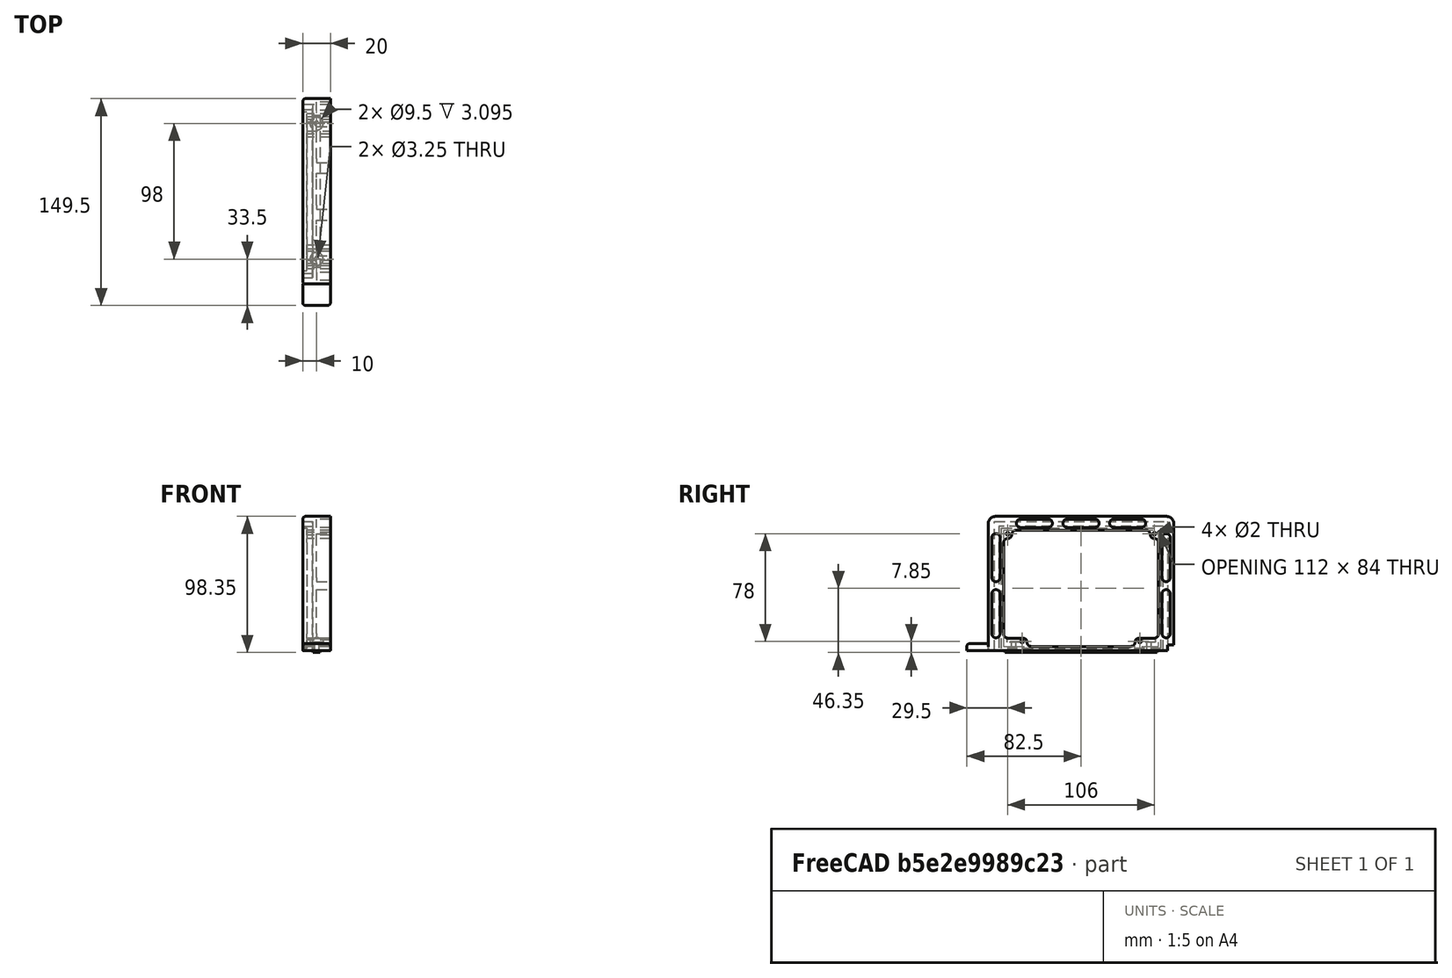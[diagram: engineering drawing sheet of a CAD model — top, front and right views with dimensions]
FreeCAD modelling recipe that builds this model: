
FCSTD DOCUMENT  (FreeCAD 0.18R)
Label: K-MINI-Enclosure-TopHandleV2
License: CreativeCommons Attribution
LicenseURL: http://creativecommons.org/licenses/by/4.0/
objects: Sketcher::SketchObject×8, PartDesign::Pocket×4, PartDesign::Pad×3, PartDesign::Fillet×2, PartDesign::Body×2, Mesh::Feature×2, PartDesign::Hole×1, Part::Mirroring×1, Part::MultiFuse×1, App::Part×1
note: 30 computed .brp shape members not serialized (recipe doc carries the construction recipe); baked Part::Feature solids carry a one-line shape summary decoded from their .brp

FEATURE [Sketcher::SketchObject] Sketch  label="BaseProfile"
  MapMode = 5
  Placement = pos=(0,0,0) rot=(0.57735,0.57735,0.57735;2.0944rad)
  Support = -> [YZ_Plane]
  sketch-geometry (27):
    g0: LineSegment StartX=-7 StartY=0 StartZ=0 EndX=-7 EndY=92 EndZ=0
    g1: ArcOfCircle CenterX=-2 CenterY=92 CenterZ=0 NormalX=0 NormalY=0 NormalZ=1 AngleXU=0 Radius=5 StartAngle=1.5708 EndAngle=3.14159
    g2: LineSegment StartX=-2 StartY=97 StartZ=0 EndX=122 EndY=97 EndZ=0
    g3: ArcOfCircle CenterX=122 CenterY=92 CenterZ=0 NormalX=0 NormalY=0 NormalZ=1 AngleXU=0 Radius=5 StartAngle=2e-16 EndAngle=1.5708
    g4: LineSegment StartX=127 StartY=92 StartZ=0 EndX=127 EndY=4.1 EndZ=0
    g5: LineSegment StartX=122.5 StartY=0 StartZ=0 EndX=-7 EndY=0 EndZ=0
    g6: LineSegment StartX=4 StartY=12 StartZ=0 EndX=4 EndY=78 EndZ=0
    g7: LineSegment StartX=13 StartY=87 StartZ=0 EndX=107 EndY=87 EndZ=0
    g8: LineSegment StartX=116 StartY=78 StartZ=0 EndX=116 EndY=12 EndZ=0
    g9: ArcOfCircle CenterX=107 CenterY=84 CenterZ=0 NormalX=0 NormalY=0 NormalZ=1 AngleXU=0 Radius=3 StartAngle=0 EndAngle=1.5708
    g10: LineSegment [constr] StartX=60 StartY=116.041 StartZ=0 EndX=60 EndY=-23.3593 EndZ=0
    g11: LineSegment StartX=122.5 StartY=0 StartZ=0 EndX=122.5 EndY=4.1 EndZ=0
    g12: LineSegment StartX=122.5 StartY=4.1 StartZ=0 EndX=127 EndY=4.1 EndZ=0
    g13: ArcOfCircle CenterX=24 CenterY=6 CenterZ=0 NormalX=0 NormalY=0 NormalZ=1 AngleXU=0 Radius=3 StartAngle=3.14159 EndAngle=4.71239
    g14: ArcOfCircle CenterX=96 CenterY=6 CenterZ=0 NormalX=0 NormalY=0 NormalZ=1 AngleXU=0 Radius=3 StartAngle=4.71239 EndAngle=6.28319
    g15: ArcOfCircle CenterX=102 CenterY=6 CenterZ=0 NormalX=0 NormalY=0 NormalZ=1 AngleXU=0 Radius=3 StartAngle=1.5708 EndAngle=3.14159
    g16: LineSegment StartX=24 StartY=3 StartZ=0 EndX=96 EndY=3 EndZ=0
    g17: ArcOfCircle CenterX=18 CenterY=6 CenterZ=0 NormalX=0 NormalY=0 NormalZ=1 AngleXU=0 Radius=3 StartAngle=0 EndAngle=1.5708
    g18: ArcOfCircle CenterX=7 CenterY=84 CenterZ=0 NormalX=0 NormalY=0 NormalZ=1 AngleXU=0 Radius=3 StartAngle=4.71239 EndAngle=6.28319
    g19: ArcOfCircle CenterX=7 CenterY=78 CenterZ=0 NormalX=0 NormalY=0 NormalZ=1 AngleXU=0 Radius=3 StartAngle=1.5708 EndAngle=3.14159
    g20: ArcOfCircle CenterX=13 CenterY=84 CenterZ=0 NormalX=0 NormalY=0 NormalZ=1 AngleXU=0 Radius=3 StartAngle=1.5708 EndAngle=3.14159
    g21: ArcOfCircle CenterX=113 CenterY=84 CenterZ=0 NormalX=0 NormalY=0 NormalZ=1 AngleXU=0 Radius=3 StartAngle=3.14159 EndAngle=4.71239
    g22: ArcOfCircle CenterX=113 CenterY=78 CenterZ=0 NormalX=0 NormalY=0 NormalZ=1 AngleXU=0 Radius=3 StartAngle=-1.8e-15 EndAngle=1.5708
    g23: LineSegment StartX=102 StartY=9 StartZ=0 EndX=113 EndY=9 EndZ=0
    g24: ArcOfCircle CenterX=113 CenterY=12 CenterZ=0 NormalX=0 NormalY=0 NormalZ=1 AngleXU=0 Radius=3 StartAngle=4.71239 EndAngle=6.28319
    g25: LineSegment StartX=7 StartY=9 StartZ=0 EndX=18 EndY=9 EndZ=0
    g26: ArcOfCircle CenterX=7 CenterY=12 CenterZ=0 NormalX=0 NormalY=0 NormalZ=1 AngleXU=0 Radius=3 StartAngle=3.14159 EndAngle=4.71239
  constraints (70):
    c: Tangent(g0,g1) = 1.5708
    c: Tangent(g1,g2) = 1.5708
    c: Tangent(g2,g3) = 1.5708
    c: Tangent(g3,g4) = 1.5708
    c: Coincident(g5,g0)
    c: Horizontal(g2)
    c: Vertical(g0)
    c: Vertical(g4)
    c: Radius(g1) = 5
    c: Equal(g1,g3)
    c: Tangent(g7,g9) = 1.5708
    c: Vertical(g6)
    c: Vertical(g8)
    c: Horizontal(g7)
    c: DistanceX(g0,g-1) = 7
    c: Horizontal(g5)
    c: DistanceY(g-1,g1) = 97
    c: Radius(g9) = 3
    c: PointOnObject(g0,g-1)
    c: DistanceX(g-1,g10) = 60
    c: Symmetric(g6,g8,g10)
    c: Coincident(g11,g12)
    c: Coincident(g4,g12)
    c: Coincident(g5,g11)
    c: Vertical(g11)
    c: Horizontal(g12)
    c: DistanceY(g5,g11) = 4.1
    c: DistanceX(g0,g4) = 134
    c: Tangent(g15,g14) = 1.5708
    c: Tangent(g14,g16) = -1.5708
    c: Tangent(g16,g13) = -1.5708
    c: Horizontal(g16)
    c: DistanceX(g12,g12) = 4.5
    c: Horizontal(g17,g17)
    c: Vertical(g17,g17)
    c: Tangent(g17,g13) = 1.5708
    c: Equal(g13,g17)
    c: Horizontal(g14,g15)
    c: Equal(g15,g14)
    c: Horizontal(g18,g18)
    c: Vertical(g18,g18)
    c: Tangent(g19,g6) = 1.5708
    c: Tangent(g19,g18) = 1.5708
    c: Equal(g19,g18)
    c: Tangent(g7,g20) = 1.5708
    c: Tangent(g18,g20) = 1.5708
    c: Equal(g18,g20)
    c: Equal(g13,g14)
    c: Tangent(g22,g8) = 1.5708
    c: Vertical(g21,g21)
    c: Horizontal(g21,g21)
    c: Tangent(g21,g22) = 1.5708
    c: Tangent(g9,g21) = 1.5708
    c: Equal(g9,g21)
    c: Equal(g21,g22)
    c: Tangent(g15,g23) = 1.5708
    c: Horizontal(g23)
    c: Tangent(g23,g24) = -1.5708
    c: Tangent(g8,g24) = 1.5708
    c: Equal(g15,g24)
    c: Tangent(g25,g17) = 1.5708
    c: Tangent(g6,g26) = 1.5708
    c: Tangent(g25,g26) = -1.5708
    c: Symmetric(g13,g14,g10)
    c: DistanceY(g0,g7) = 87
    c: DistanceX(g6,g8) = 112
    c: Equal(g20,g9)
    c: DistanceY(g-1,g13) = 3
    c: DistanceX(g25,g25) = 11
    c: Radius(g24) = 3
FEATURE [PartDesign::Pad] Pad  label="RawHandle"
  Length = 20
  Length2 = 100
  Placement = pos=(0,0,0) rot=(0.57735,0.57735,0.57735;2.0944rad)
  Profile = -> Sketch
  Type = 0
FEATURE [Sketcher::SketchObject] Sketch001  label="TopFRCutoutProfile"
  MapMode = 5
  Placement = pos=(20,-1.8e-14,1.1e-14) rot=(0.57735,0.57735,0.57735;2.0944rad)
  sketch-geometry (9):
    g0: LineSegment StartX=-2.5 StartY=0 StartZ=0 EndX=-2.5 EndY=93.2 EndZ=0
    g1: LineSegment StartX=-2.5 StartY=93.2 StartZ=0 EndX=122.5 EndY=93.2 EndZ=0
    g2: LineSegment StartX=122.5 StartY=93.2 StartZ=0 EndX=122.5 EndY=0 EndZ=0
    g3: LineSegment StartX=122.5 StartY=0 StartZ=0 EndX=119.3 EndY=0 EndZ=0
    g4: LineSegment StartX=119.3 StartY=0 StartZ=0 EndX=119.3 EndY=90 EndZ=0
    g5: LineSegment StartX=119.3 StartY=90 StartZ=0 EndX=0.7 EndY=90 EndZ=0
    g6: LineSegment StartX=0.7 StartY=90 StartZ=0 EndX=0.7 EndY=0 EndZ=0
    g7: LineSegment StartX=0.7 StartY=0 StartZ=0 EndX=-2.5 EndY=0 EndZ=0
    g8: LineSegment [constr] StartX=60 StartY=110 StartZ=0 EndX=60 EndY=0 EndZ=0
  constraints (26):
    c: Coincident(g0,g1)
    c: Coincident(g1,g2)
    c: Coincident(g2,g3)
    c: Coincident(g3,g4)
    c: Coincident(g4,g5)
    c: Coincident(g5,g6)
    c: Coincident(g6,g7)
    c: Horizontal(g7)
    c: Horizontal(g3)
    c: Horizontal(g1)
    c: Horizontal(g5)
    c: Vertical(g0)
    c: Vertical(g6)
    c: Vertical(g4)
    c: Vertical(g2)
    c: DistanceY(g4,g1) = 3.2
    c: DistanceX(g3,g3) = 3.2
    c: DistanceY(g6,g5) = 90
    c: DistanceX(g0,g2) = 125  'coverwidth'
    c: DistanceX(g-1,g8) = 60
    c: Coincident(g0,g7)
    c: PointOnObject(g6,g-1)
    c: Symmetric(g6,g3,g8)
    c: Symmetric(g0,g2,g8)
    c: PointOnObject(g8,g-1)
    c: DistanceY(g8,g8) = 110
FEATURE [PartDesign::Pocket] Pocket  label="TopFRPanelMount"
  BaseFeature = -> Pad
  Length = 7
  Length2 = 100
  Placement = pos=(0,0,0) rot=(0.57735,0.57735,0.57735;2.0944rad)
  Profile = -> Sketch001
  Type = 0
FEATURE [Sketcher::SketchObject] Sketch002  label="SlotProfile"
  Placement = pos=(0,0,-1.04e-13) rot=(0.707107,0.707107,0;3.14159rad)
  sketch-geometry (4):
    g0: LineSegment StartX=5 StartY=12.5 StartZ=0 EndX=115 EndY=12.5 EndZ=0
    g1: LineSegment StartX=115 StartY=12.5 StartZ=0 EndX=115 EndY=7.5 EndZ=0
    g2: LineSegment StartX=115 StartY=7.5 StartZ=0 EndX=5 EndY=7.5 EndZ=0
    g3: LineSegment StartX=5 StartY=7.5 StartZ=0 EndX=5 EndY=12.5 EndZ=0
  constraints (12):
    c: Coincident(g0,g1)
    c: Coincident(g1,g2)
    c: Coincident(g2,g3)
    c: Coincident(g3,g0)
    c: Horizontal(g0)
    c: Horizontal(g2)
    c: Vertical(g1)
    c: Vertical(g3)
    c: DistanceX(g-1,g2) = 5
    c: DistanceX(g2,g2) = 110
    c: DistanceY(g3,g3) = 5
    c: DistanceY(g-1,g2) = 7.5
FEATURE [Sketcher::SketchObject] Sketch004  label="M2Screwpositions"
  MapMode = 5
  Placement = pos=(20,-2.7e-14,1.6e-14) rot=(0.57735,0.57735,0.57735;2.0944rad)
  sketch-geometry (5):
    g0: Circle CenterX=7 CenterY=84.5 CenterZ=0 NormalX=0 NormalY=0 NormalZ=1 AngleXU=0 Radius=1
    g1: Circle CenterX=113 CenterY=84.5 CenterZ=0 NormalX=0 NormalY=0 NormalZ=1 AngleXU=0 Radius=1
    g2: Circle CenterX=17.5 CenterY=6.5 CenterZ=0 NormalX=0 NormalY=0 NormalZ=1 AngleXU=0 Radius=1
    g3: Circle CenterX=102.5 CenterY=6.5 CenterZ=0 NormalX=0 NormalY=0 NormalZ=1 AngleXU=0 Radius=1
    g4: LineSegment [constr] StartX=60 StartY=121.121 StartZ=0 EndX=60 EndY=-12.2493 EndZ=0
  constraints (11):
    c: Radius(g0) = 1
    c: Equal(g0,g1)
    c: Equal(g0,g2)
    c: DistanceY(g-1,g2) = 6.5
    c: DistanceY(g2,g0) = 78
    c: Horizontal(g0,g1)
    c: DistanceX(g-1,g4) = 60
    c: Symmetric(g2,g3,g4)
    c: DistanceX(g0,g1) = 106
    c: DistanceX(g2,g3) = 85
    c: Symmetric(g1,g0,g4)
FEATURE [Sketcher::SketchObject] Sketch005  label="Ovals"
  MapMode = 5
  Placement = pos=(0,0,0) rot=(0.57735,0.57735,-0.57735;4.18879rad)
  Support = -> [Pocket]
  sketch-geometry (29):
    g0: ArcOfCircle CenterX=-1.5 CenterY=-12.2603 CenterZ=0 NormalX=0 NormalY=0 NormalZ=1 AngleXU=0 Radius=3 StartAngle=3e-16 EndAngle=3.14159
    g1: ArcOfCircle CenterX=-1.5 CenterY=-41.0407 CenterZ=0 NormalX=0 NormalY=0 NormalZ=1 AngleXU=0 Radius=3 StartAngle=3.14159 EndAngle=6.28319
    g2: LineSegment StartX=-4.5 StartY=-12.2603 StartZ=0 EndX=-4.5 EndY=-41.0407 EndZ=0
    g3: LineSegment StartX=1.5 StartY=-12.2603 StartZ=0 EndX=1.5 EndY=-41.0407 EndZ=0
    g4: ArcOfCircle CenterX=-1.5 CenterY=-52.7873 CenterZ=0 NormalX=0 NormalY=0 NormalZ=1 AngleXU=0 Radius=3 StartAngle=-9e-16 EndAngle=3.14159
    g5: ArcOfCircle CenterX=-1.5 CenterY=-81.5678 CenterZ=0 NormalX=0 NormalY=0 NormalZ=1 AngleXU=0 Radius=3 StartAngle=3.14159 EndAngle=6.28319
    g6: LineSegment StartX=-4.5 StartY=-52.7873 StartZ=0 EndX=-4.5 EndY=-81.5678 EndZ=0
    g7: LineSegment StartX=1.5 StartY=-52.7873 StartZ=0 EndX=1.5 EndY=-81.5678 EndZ=0
    g8: ArcOfCircle CenterX=16.2869 CenterY=-92 CenterZ=0 NormalX=0 NormalY=0 NormalZ=1 AngleXU=0 Radius=3 StartAngle=1.5708 EndAngle=4.71239
    g9: ArcOfCircle CenterX=36.2869 CenterY=-92 CenterZ=0 NormalX=0 NormalY=0 NormalZ=1 AngleXU=0 Radius=3 StartAngle=4.71239 EndAngle=7.85398
    g10: LineSegment StartX=16.2869 StartY=-95 StartZ=0 EndX=36.2869 EndY=-95 EndZ=0
    g11: LineSegment StartX=16.2869 StartY=-89 StartZ=0 EndX=36.2869 EndY=-89 EndZ=0
    g12: ArcOfCircle CenterX=50 CenterY=-92 CenterZ=0 NormalX=0 NormalY=0 NormalZ=1 AngleXU=0 Radius=3 StartAngle=1.5708 EndAngle=4.71239
    g13: ArcOfCircle CenterX=70 CenterY=-92 CenterZ=0 NormalX=0 NormalY=0 NormalZ=1 AngleXU=0 Radius=3 StartAngle=4.71239 EndAngle=7.85398
    g14: LineSegment StartX=50 StartY=-95 StartZ=0 EndX=70 EndY=-95 EndZ=0
    g15: LineSegment StartX=50 StartY=-89 StartZ=0 EndX=70 EndY=-89 EndZ=0
    g16: ArcOfCircle CenterX=83.7131 CenterY=-92 CenterZ=0 NormalX=0 NormalY=0 NormalZ=1 AngleXU=0 Radius=3 StartAngle=1.5708 EndAngle=4.71239
    g17: ArcOfCircle CenterX=103.713 CenterY=-92 CenterZ=0 NormalX=0 NormalY=0 NormalZ=1 AngleXU=0 Radius=3 StartAngle=4.71239 EndAngle=7.85398
    g18: LineSegment StartX=83.7131 StartY=-95 StartZ=0 EndX=103.713 EndY=-95 EndZ=0
    g19: LineSegment StartX=83.7131 StartY=-89 StartZ=0 EndX=103.713 EndY=-89 EndZ=0
    g20: ArcOfCircle CenterX=121.5 CenterY=-81.5678 CenterZ=0 NormalX=0 NormalY=0 NormalZ=1 AngleXU=0 Radius=3 StartAngle=3.14159 EndAngle=6.28319
    g21: ArcOfCircle CenterX=121.5 CenterY=-52.7873 CenterZ=0 NormalX=0 NormalY=0 NormalZ=1 AngleXU=0 Radius=3 StartAngle=2e-16 EndAngle=3.14159
    g22: LineSegment StartX=124.5 StartY=-81.5678 StartZ=0 EndX=124.5 EndY=-52.7873 EndZ=0
    g23: LineSegment StartX=118.5 StartY=-81.5678 StartZ=0 EndX=118.5 EndY=-52.7873 EndZ=0
    g24: ArcOfCircle CenterX=121.5 CenterY=-41.0407 CenterZ=0 NormalX=0 NormalY=0 NormalZ=1 AngleXU=0 Radius=3 StartAngle=3.14159 EndAngle=6.28319
    g25: ArcOfCircle CenterX=121.5 CenterY=-12.2603 CenterZ=0 NormalX=0 NormalY=0 NormalZ=1 AngleXU=0 Radius=3 StartAngle=0 EndAngle=3.14159
    g26: LineSegment StartX=124.5 StartY=-41.0407 StartZ=0 EndX=124.5 EndY=-12.2603 EndZ=0
    g27: LineSegment StartX=118.5 StartY=-41.0407 StartZ=0 EndX=118.5 EndY=-12.2603 EndZ=0
    g28: LineSegment [constr] StartX=60 StartY=32.8445 StartZ=0 EndX=60 EndY=-124.528 EndZ=0
  constraints (65):
    c: Tangent(g0,g3) = 1.5708
    c: Tangent(g0,g2) = -1.5708
    c: Tangent(g2,g1) = -1.5708
    c: Tangent(g3,g1) = 1.5708
    c: Vertical(g2)
    c: Equal(g0,g1)
    c: Tangent(g4,g7) = 1.5708
    c: Tangent(g4,g6) = -1.5708
    c: Tangent(g6,g5) = -1.5708
    c: Tangent(g7,g5) = 1.5708
    c: Vertical(g6)
    c: Equal(g4,g5)
    c: Tangent(g8,g11) = 1.5708
    c: Tangent(g8,g10) = -1.5708
    c: Tangent(g10,g9) = -1.5708
    c: Tangent(g11,g9) = 1.5708
    c: Horizontal(g10)
    c: Equal(g8,g9)
    c: Tangent(g12,g15) = 1.5708
    c: Tangent(g12,g14) = -1.5708
    c: Tangent(g14,g13) = -1.5708
    c: Tangent(g15,g13) = 1.5708
    c: Horizontal(g14)
    c: Equal(g12,g13)
    c: Tangent(g16,g19) = 1.5708
    c: Tangent(g16,g18) = -1.5708
    c: Tangent(g18,g17) = -1.5708
    c: Tangent(g19,g17) = 1.5708
    c: Horizontal(g18)
    c: Equal(g16,g17)
    c: Tangent(g20,g23) = 1.5708
    c: Tangent(g20,g22) = -1.5708
    c: Tangent(g22,g21) = -1.5708
    c: Tangent(g23,g21) = 1.5708
    c: Vertical(g22)
    c: Equal(g20,g21)
    c: Tangent(g24,g27) = 1.5708
    c: Tangent(g24,g26) = -1.5708
    c: Tangent(g26,g25) = -1.5708
    c: Tangent(g27,g25) = 1.5708
    c: Vertical(g26)
    c: Equal(g24,g25)
    c: Horizontal(g8,g12)
    c: Vertical(g0,g4)
    c: Vertical(g25,g21)
    c: Equal(g3,g7)
    c: Equal(g7,g27)
    c: Equal(g27,g23)
    c: Radius(g5) = 3
    c: Equal(g5,g1)
    c: Equal(g5,g24)
    c: Equal(g5,g20)
    c: Horizontal(g5,g20)
    c: DistanceX(g-1,g28) = 60
    c: Symmetric(g0,g25,g28)
    c: Symmetric(g13,g12,g28)
    c: Symmetric(g9,g16,g28)
    c: Equal(g10,g18)
    c: Equal(g18,g14)
    c: Radius(g9) = 3
    c: Equal(g9,g13)
    c: Equal(g9,g17)
    c: DistanceY(g8,g-1) = 92
    c: DistanceX(g0,g25) = 123
    c: DistanceX(g12,g13) = 20
FEATURE [PartDesign::Pocket] Pocket003  label="DesignElements"
  BaseFeature = -> Pocket
  Length = 10
  Length2 = 100
  Placement = pos=(0,0,0) rot=(0.57735,0.57735,0.57735;2.0944rad)
  Profile = -> Sketch005
  Type = 0
FEATURE [PartDesign::Pad] Pad001  label="SlotRail"
  BaseFeature = -> Pocket003
  Length = 1.35
  Length2 = 100
  Placement = pos=(0,0,0) rot=(0.57735,0.57735,0.57735;2.0944rad)
  Profile = -> Sketch002
  Type = 0
FEATURE [PartDesign::Pocket] Pocket004  label="M2Holes"
  BaseFeature = -> Pad001
  Length = 20
  Length2 = 100
  Placement = pos=(0,0,0) rot=(0.57735,0.57735,0.57735;2.0944rad)
  Profile = -> Sketch004
  Type = 0
FEATURE [Sketcher::SketchObject] Sketch003  label="SideCoverArea"
  MapMode = 5
  Placement = pos=(20,-4.4e-15,4.4e-15) rot=(0.57735,0.57735,0.57735;2.0944rad)
  Support = -> [Pocket004]
  sketch-geometry (5):
    g0: LineSegment StartX=2.5 StartY=88.5 StartZ=0 EndX=117.5 EndY=88.5 EndZ=0
    g1: LineSegment StartX=117.5 StartY=88.5 StartZ=0 EndX=117.5 EndY=1.5 EndZ=0
    g2: LineSegment StartX=117.5 StartY=1.5 StartZ=0 EndX=2.5 EndY=1.5 EndZ=0
    g3: LineSegment StartX=2.5 StartY=1.5 StartZ=0 EndX=2.5 EndY=88.5 EndZ=0
    g4: LineSegment [constr] StartX=60 StartY=123.567 StartZ=0 EndX=60 EndY=-13.9522 EndZ=0
  constraints (13):
    c: Coincident(g0,g1)
    c: Coincident(g1,g2)
    c: Coincident(g2,g3)
    c: Coincident(g3,g0)
    c: Horizontal(g0)
    c: Horizontal(g2)
    c: Vertical(g1)
    c: Vertical(g3)
    c: DistanceX(g2,g2) = 115
    c: DistanceY(g-1,g2) = 1.5
    c: DistanceY(g3,g3) = 87
    c: DistanceX(g-1,g4) = 60
    c: Symmetric(g0,g0,g4)
FEATURE [PartDesign::Pocket] Pocket005  label="SideCoverCutout"
  BaseFeature = -> Pocket004
  Length = 3
  Length2 = 100
  Placement = pos=(0,0,0) rot=(0.57735,0.57735,0.57735;2.0944rad)
  Profile = -> Sketch003
  Type = 0
FEATURE [Sketcher::SketchObject] Sketch006  label="ExtrusionScrewPos"
  Placement = pos=(0,3e-15,10) rot=(0,0,-1;1.5708rad)
  Support = -> [Pocket004]
  sketch-geometry (3):
    g0: LineSegment [constr] StartX=-60 StartY=94.2757 StartZ=0 EndX=-60 EndY=-53.0118 EndZ=0
    g1: Circle CenterX=-109 CenterY=10 CenterZ=0 NormalX=0 NormalY=0 NormalZ=1 AngleXU=0 Radius=1.75
    g2: Circle CenterX=-11 CenterY=10 CenterZ=0 NormalX=0 NormalY=0 NormalZ=1 AngleXU=0 Radius=1.75
  constraints (7):
    c: Vertical(g0)
    c: Radius(g1) = 1.75
    c: Equal(g1,g2)
    c: Symmetric(g1,g2,g0)
    c: DistanceY(g-1,g1) = 10
    c: DistanceX(g1,g2) = 98
    c: DistanceX(g0,g-1) = 60
FEATURE [PartDesign::Hole] Hole
  BaseFeature = -> Pocket005
  Depth = 25
  DepthType = 0
  Diameter = 3.25
  DrillPoint = 1
  DrillPointAngle = 118
  HoleCutCountersinkAngle = 90
  HoleCutDepth = 4
  HoleCutDiameter = 9.5
  HoleCutType = 1
  ModelActualThread = false
  Placement = pos=(0,0,0) rot=(0.57735,0.57735,0.57735;2.0944rad)
  Profile = -> Sketch006
  Tapered = false
  TaperedAngle = 90
  ThreadAngle = 0
  ThreadClass = 0
  ThreadCutOffInner = 0
  ThreadCutOffOuter = 0
  ThreadDirection = 0
  ThreadFit = 0
  ThreadPitch = 0
  ThreadSize = 0
  ThreadType = 0
  Threaded = false
FEATURE [Sketcher::SketchObject] Sketch007
  MapMode = 5
  Placement = pos=(0,0,0) rot=(0.57735,0.57735,0.57735;2.0944rad)
  Support = -> [YZ_Plane002]
  sketch-geometry (5):
    g0: LineSegment StartX=-7 StartY=0 StartZ=0 EndX=-22.5 EndY=0 EndZ=0
    g1: LineSegment StartX=-22.5 StartY=0 StartZ=0 EndX=-22.5 EndY=3 EndZ=0
    g2: ArcOfCircle CenterX=-20.5 CenterY=3 CenterZ=0 NormalX=0 NormalY=0 NormalZ=1 AngleXU=0 Radius=2 StartAngle=1.5708 EndAngle=3.14159
    g3: LineSegment StartX=-20.5 StartY=5 StartZ=0 EndX=-7 EndY=5 EndZ=0
    g4: LineSegment StartX=-7 StartY=5 StartZ=0 EndX=-7 EndY=0 EndZ=0
  constraints (14):
    c: Coincident(g0,g1)
    c: Tangent(g1,g2) = 1.5708
    c: Tangent(g2,g3) = 1.5708
    c: Coincident(g3,g4)
    c: Coincident(g4,g0)
    c: Vertical(g4)
    c: Horizontal(g3)
    c: Vertical(g1)
    c: Horizontal(g0)
    c: PointOnObject(g0,g-1)
    c: DistanceX(g0,g-1) = 7
    c: DistanceY(g-1,g3) = 5
    c: DistanceX(g0,g-1) = 22.5
    c: Radius(g2) = 2
FEATURE [PartDesign::Pad] Pad002
  Length = 20
  Length2 = 100
  Placement = pos=(0,0,0) rot=(0.57735,0.57735,0.57735;2.0944rad)
  Profile = -> Sketch007
  Type = 0
FEATURE [PartDesign::Fillet] Fillet
  Base = -> Pad002 [Edge7,Edge12]
  BaseFeature = -> Pad002
  Placement = pos=(0,0,0) rot=(0.57735,0.57735,0.57735;2.0944rad)
  Radius = 2
FEATURE [PartDesign::Body] Body001  label="VBarCover"
  Group = -> [Sketch007,Pad002,Fillet]
  Origin = -> Origin002
  Placement = pos=(360,0,0) rot=(0,0,1;0rad)
  Tip = -> Fillet
FEATURE [PartDesign::Fillet] Fillet001
  Base = -> Hole [Edge84]
  BaseFeature = -> Hole
  Placement = pos=(0,0,0) rot=(0.57735,0.57735,0.57735;2.0944rad)
  Radius = 2
FEATURE [PartDesign::Body] Body  label="HandleL"
  Group = -> [Sketch,Pad,Sketch001,Pocket,Sketch002,Sketch003,Sketch004,Sketch005,Pocket003,Pad001,Pocket004,Pocket005,Sketch006,Hole,Fillet001]
  Origin = -> Origin
  Tip = -> Fillet001
FEATURE [Part::Mirroring] Part__Mirroring  label="HandleL (Mirror #1)"
  Base = (190,0,0)
  Normal = (1,0,0)
  Source = -> Body
FEATURE [Part::MultiFuse] Fusion  label="HandleR"
  Shapes = -> [Part__Mirroring,Body001]
FEATURE [App::Part] Part
  Group = -> [Body,Body001,Part__Mirroring,Fusion]
  Origin = -> Origin001
FEATURE [Mesh::Feature] Mesh  label="HandleL (Meshed)"
  Placement = pos=(0,0,0) rot=(0,1,0;4.71239rad)
FEATURE [Mesh::Feature] Mesh001  label="HandleR (Meshed)"
  Placement = pos=(0,0,0) rot=(0,1,0;1.5708rad)
